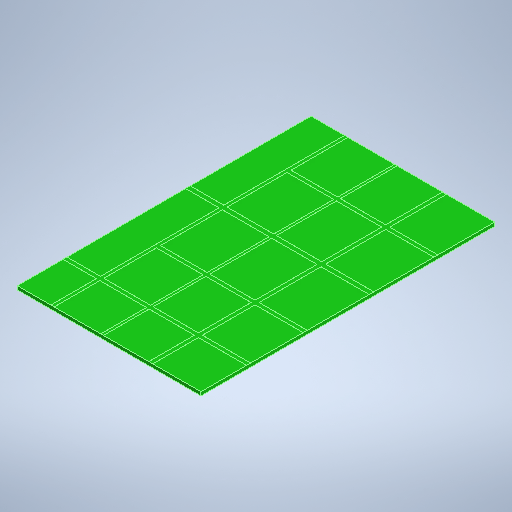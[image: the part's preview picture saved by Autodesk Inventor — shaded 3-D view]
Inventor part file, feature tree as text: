
AUTODESK INVENTOR PART (.ipt)
format: ipt  version: 2025.2 (Build 292293000, 293)  size: 298,496 bytes
history: native  units: mm
features: extrude x2, sketch x2, other x1
ambient origin geometry x8: Origin, YZ Plane, XZ Plane, XY Plane, X Axis, Y Axis, Z Axis, Center Point
bodies: Body1 (feature_tree)
feature tree (5):
  other  "Sólido1"
  extrude  "Extrusión1"  Depth=800.0mm
  extrude  "Extrusión3"  Depth=0.1mm TaperAngle=0.0deg
  sketch  "Boceto1"  dims[d0=500.0mm d1=800.0mm]
  sketch  "Boceto3"  dims[d2=10.0mm d3=0.0mm d6=0.1mm d7=0.0mm]
